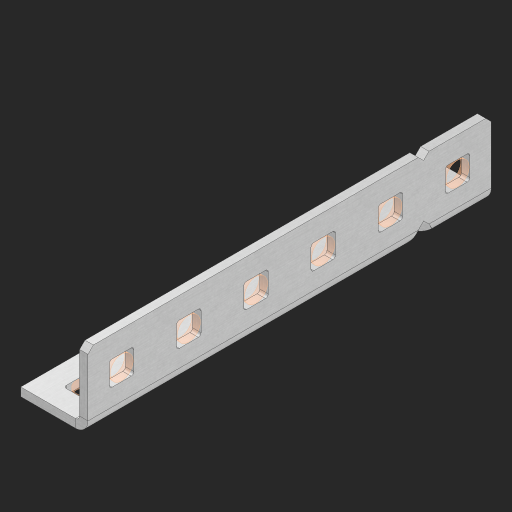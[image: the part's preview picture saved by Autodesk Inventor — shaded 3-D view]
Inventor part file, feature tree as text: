
AUTODESK INVENTOR PART (.ipt)
format: ipt  version: 2023 (Build 270158000, 158)  size: 519,168 bytes
history: native  units: in
note: dims shown in document units (in); Inventor stores cm internally (conversion verified against a paired STEP export)
features: other x17, extrude x11, sheet_metal_op x10, sketch x8, mirror x1, pattern_linear x1, chamfer x1
ambient origin geometry x8: Origin, YZ Plane, XZ Plane, XY Plane, X Axis, Y Axis, Z Axis, Center Point
bodies: Solid1 (feature_tree), Body (feature_tree)
feature tree (49):
  other  "Flange Pattern Plane"
  sheet_metal_op  "Flange Pattern"
  sheet_metal_op  "Body Pattern"
  other  "Arc Length"
  mirror  "Notch Mirror"
  pattern_linear  "Notch Pattern"  Spacing1=0.25in  [1 undecoded]
  chamfer  "End Chamfer"
  extrude  "Half Cut"  Depth=0.0625in
  sketch  "Sketch1"  dims[d0=1.5in]
  other  "Plate1"
  sketch  "Sketch2"  dims[d1=3.0in]
  other  "Plate2"
  sheet_metal_op  "Bend1"
  sheet_metal_op  "Corner1"
  sketch  "Sketch3"  dims[d2=0.0625in]
  other  "Flange Pattern Sketch"
  sketch  "Sketch7"  dims[d3=0.0625in]
  other  "Srf1"
  other  "Srf2"
  sketch  "Sketch8"  dims[d4=0.0312in]
  sketch  "Sketch9"  dims[d5=0.125in]
  other  "Srf91"
  sheet_metal_op  "Body Pattern Sketch"
  other  "Srf92"
  sketch  "Sketch13"  dims[d6=0.0625in]
  sketch  "Sketch14"  dims[d7=0.5in d8=90.0deg d9=0.0312in d10=0.25in d11=0.0625in d12=0.0625in d16=0.182in d17=0.02in d18=0.0625in d19=0.0in d20=0.25in d21=0.25in d46=0.172in d47=1.0in d48=0.0in d49=0.182in d50=0.02in d51=0.25in d52=0.25in d53=0.0625in d54=0.0in d55=0.172in d56=1.0in d57=0.0in d60=2.3622in d62=0.5in d63=0.3937in d65=0.5in d85=0.1473in d86=0.1782in d88=0.04in d89=0.0625in d90=0.0in d91=0.04in d92=0.0491in d95=2.5in d96=0.04in d97=0.25in d98=45.0deg d101=0.0in d102=2.497in d131=0.5in d132=2.3622in d134=0.5in d139=0.5in]
  other  "Srf856"
  other  "Srf1310"
  other  "Srf1311"
  other  "Srf1312"
  other  "Srf1376"
  other  "Srf1377"
  other  "Srf1728"
  other  "Srf1755"
  sheet_metal_op  "Flange Stamp"
  sheet_metal_op  "Flange Circle"
  sheet_metal_op  "Body Stamp"
  sheet_metal_op  "Body Circle"
  sheet_metal_op  "Notch"
  extrude  "ExtrusionSrf2"  Depth=0.0625in
  extrude  "ExtrusionSrf92"  Depth=0.5in
  extrude  "ExtrusionSrf856"  Depth=0.02in
  extrude  "ExtrusionSrf1310"  Depth=0.0625in
  extrude  "ExtrusionSrf1311"  TaperAngle=0.0deg  [1 undecoded]
  extrude  "ExtrusionSrf1312"  Depth=0.5in
  extrude  "ExtrusionSrf1376"  Depth=0.5in
  extrude  "ExtrusionSrf1377"  Depth=0.5in
  extrude  "ExtrusionSrf1728"  Depth=0.5in TaperAngle=0.0deg
  extrude  "ExtrusionSrf1755"  Depth=0.5in
note: 2 required parameter values undecoded (feature->parameter linkage not recoverable at this tier; creation-order binding heuristic only, values carry confidence <= 0.55)
